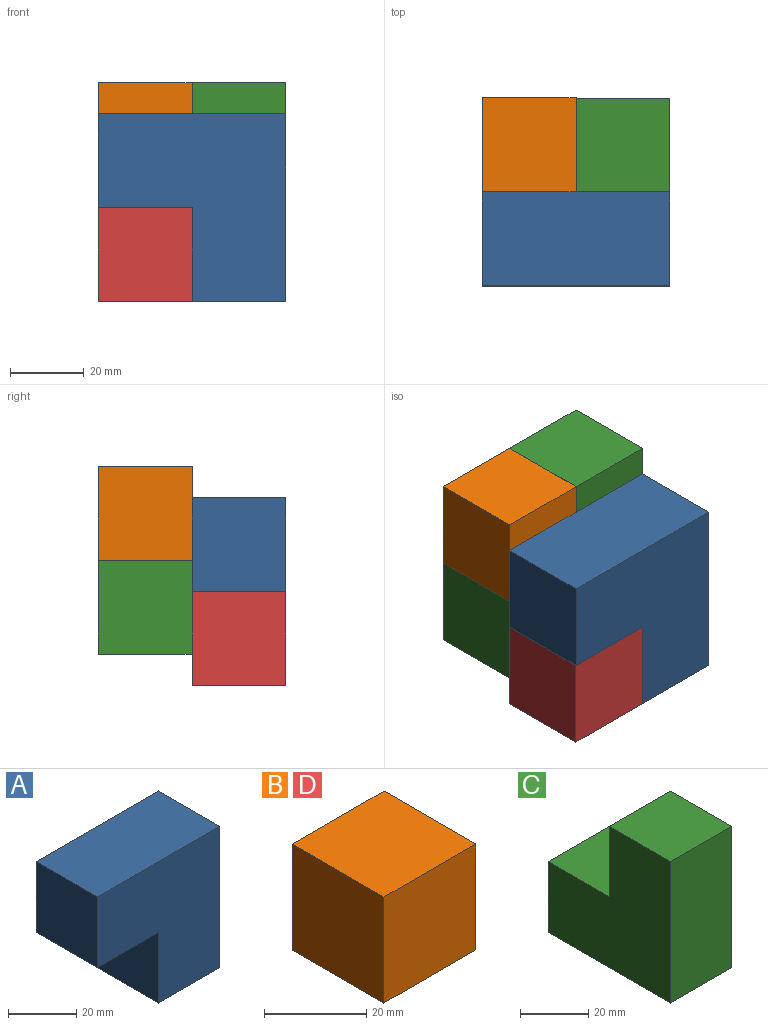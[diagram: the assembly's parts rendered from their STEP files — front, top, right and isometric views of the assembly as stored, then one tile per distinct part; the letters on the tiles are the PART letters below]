
ASSEMBLY  parts=4 mates=3
PART A: 8 faces, bbox 50.8x25.4x50.8 mm
  f0: plane 25.4x25.4mm, normal (0,0,-1), area 645.2mm2, adj f1,f5,f6,f7
  f1: plane 50.8x25.4mm, normal (1,0,0), area 1290.3mm2, adj f0,f2,f6,f7
  f2: plane 50.8x25.4mm, normal (0,0,1), area 1290.3mm2, adj f1,f3,f6,f7
  f3: plane 25.4x25.4mm, normal (-1,0,0), area 645.2mm2, adj f2,f4,f6,f7
  f4: plane 25.4x25.4mm, normal (0,0,-1), area 645.2mm2, adj f3,f5,f6,f7
  f5: plane 25.4x25.4mm, normal (-1,0,0), area 645.2mm2, adj f0,f4,f6,f7
  f6: plane 50.8x50.8mm, normal (0,-1,0), area 1935.5mm2, adj f0,f1,f2,f3,f4,f5
  f7: plane 50.8x50.8mm, normal (0,1,0), area 1935.5mm2, adj f0,f1,f2,f3,f4,f5
PART B: 6 faces, bbox 25.5x25.4x25.4 mm
  f0: plane 25.4x25.4mm, normal (1,0,0), area 645.2mm2, adj f1,f3,f4,f5
  f1: plane 25.46x25.4mm, normal (0,0,1), area 646.7mm2, adj f0,f2,f4,f5
  f2: plane 25.4x25.4mm, normal (-1,0,0), area 645.2mm2, adj f1,f3,f4,f5
  f3: plane 25.46x25.4mm, normal (0,0,-1), area 646.7mm2, adj f0,f2,f4,f5
  f4: plane 25.46x25.4mm, normal (0,-1,0), area 646.7mm2, adj f0,f1,f2,f3
  f5: plane 25.46x25.4mm, normal (0,1,0), area 646.7mm2, adj f0,f1,f2,f3
PART C: 8 faces, bbox 25.4x50.8x50.8 mm
  f0: plane 25.4x25.4mm, normal (0,0,1), area 645.2mm2, adj f1,f5,f6,f7
  f1: plane 25.4x25.4mm, normal (0,1,0), area 645.2mm2, adj f0,f2,f6,f7
  f2: plane 25.4x25.4mm, normal (0,0,1), area 645.2mm2, adj f1,f3,f6,f7
  f3: plane 50.8x25.4mm, normal (0,-1,0), area 1290.3mm2, adj f2,f4,f6,f7
  f4: plane 50.8x25.4mm, normal (0,0,-1), area 1290.3mm2, adj f3,f5,f6,f7
  f5: plane 25.4x25.4mm, normal (0,1,0), area 645.2mm2, adj f0,f4,f6,f7
  f6: plane 50.8x50.8mm, normal (1,0,0), area 1935.5mm2, adj f0,f1,f2,f3,f4,f5
  f7: plane 50.8x50.8mm, normal (-1,0,0), area 1935.5mm2, adj f0,f1,f2,f3,f4,f5
PART D: same geometry as B
PLACE A t=(-24.03,-16.71,0.52)mm
PLACE B rot(axis=(0.58,0.58,0.58),120deg) t=(-49.43,8.73,34.39)mm
PLACE C rot(axis=(0.58,-0.58,-0.58),120deg) t=(-49.43,8.69,-16.41)mm
PLACE D t=(-24,-16.71,-24.88)mm fixed
MATE fastened A.f7 <-> C.f6  axis (0,1,0) through (-19.79,-16.71,4.76)mm
MATE fastened A.f4 <-> D.f1  axis (0,0,-1) through (-36.73,-29.41,0.52)mm
MATE fastened B.f1 <-> C.f0  axis (1,0,0) through (-24.03,-4.01,21.69)mm
